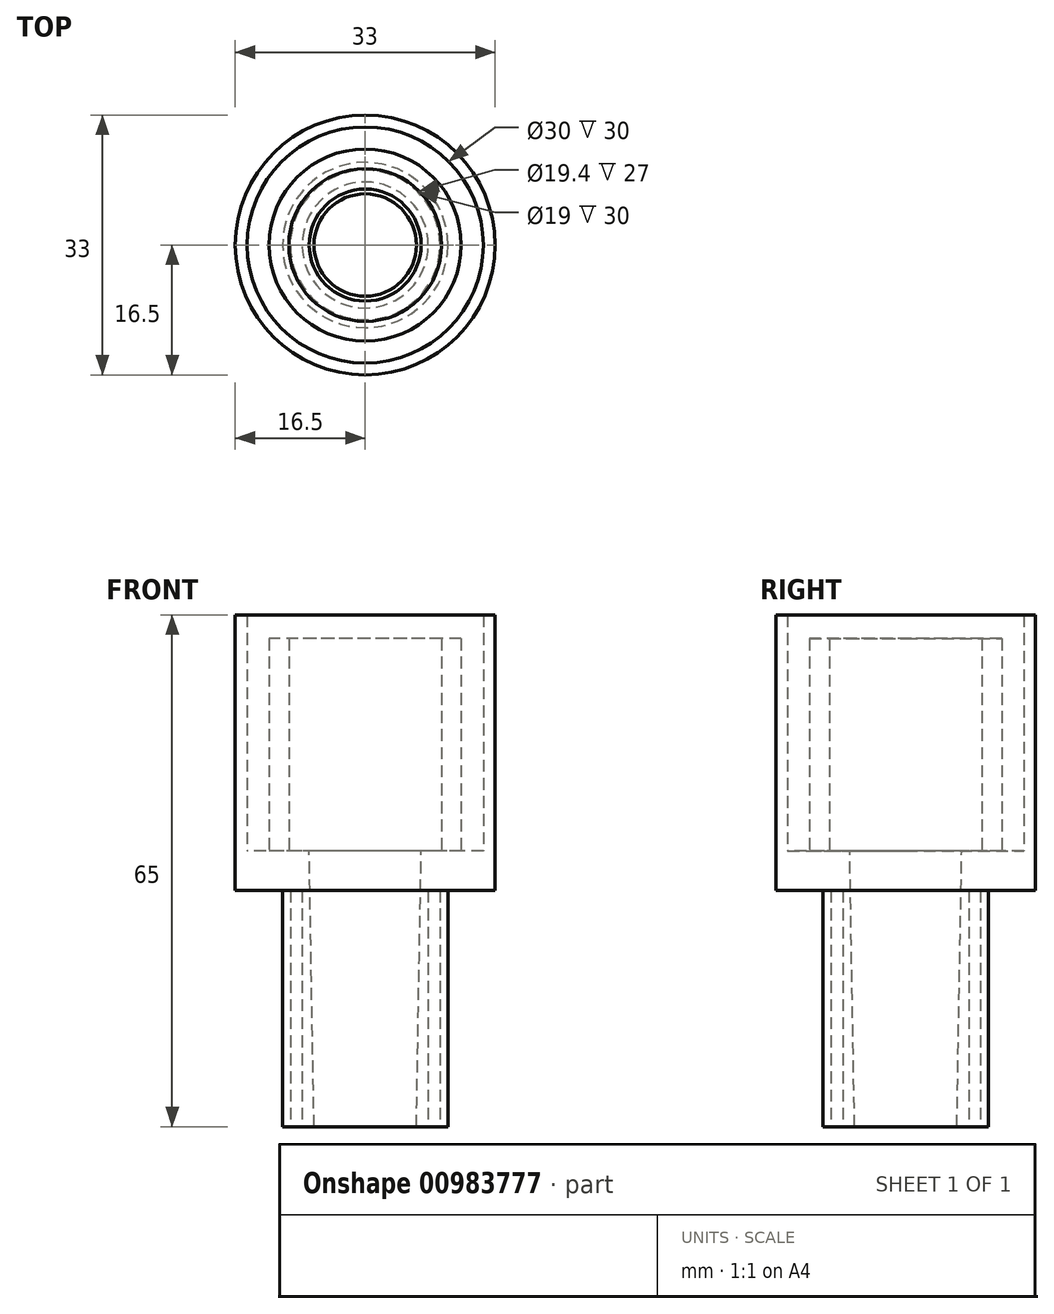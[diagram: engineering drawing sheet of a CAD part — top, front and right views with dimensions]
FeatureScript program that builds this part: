
annotation { "Feature Type Name" : "Feature", "Feature Type Description" : "" }
export const myFeature = defineFeature(function(context is Context, id is Id, definition is map)
    precondition{}
    {
        {
            var Q0;
            Q0=qCreatedBy(makeId("Top.planeOp"),FACE);
            var sketch = newSketch(context, id + "F0", { "sketchPlane" : qUnion([Q0])});
            skCircle(sketch, "E0", {"center": v(0, 0) * mm, "radius": 16.5 * mm});
            skSolve(sketch);
        }
        {
            var Q0;
            Q0 = qSketchRegion(id + "F0", true);
            extrude(context, id + "F1", {"entities" : qUnion([Q0]), "depth" : 5 * mm, "offsetDistance" : 25 * mm});
        }
        {
            var Q0;
            Q0=makeQuery(id+"F1.opExtrude","CAP_FACE",FACE,{"disambiguationData":[OSD([sQuery(id+"F0.wireOp",EDGE,"E0")])],"isStart":false});
            var sketch = newSketch(context, id + "F2", { "sketchPlane" : qUnion([Q0])});
            skCircle(sketch, "E1", {"center": v(0, 0) * mm, "radius": 15 * mm});
            skSolve(sketch);
        }
        {
            var Q0;
            Q0=makeQuery(id+"F2.imprint","IMPRINT",FACE,{"disambiguationData":[TD([[makeQuery(id+"F2.imprint","IMPRINT",EDGE,{"derivedFrom":sQuery(id+"F2.wireOp",EDGE,"E1")}),-1.0]])]});
            extrude(context, id + "F3", {"entities" : qUnion([Q0]), "operationType" : NewBodyOperationType.ADD, "depth" : 30 * mm, "offsetDistance" : 25 * mm});
        }
        {
            var Q0;
            Q0=makeQuery(id+"F1.opExtrude","CAP_FACE",FACE,{"disambiguationData":[OSD([sQuery(id+"F0.wireOp",EDGE,"E0")])],"isStart":false});
            var sketch = newSketch(context, id + "F4", { "sketchPlane" : qUnion([Q0])});
            skCircle(sketch, "E2", {"center": v(0, 0) * mm, "radius": 12.2 * mm});
            skCircle(sketch, "E3", {"center": v(0, 0) * mm, "radius": 9.7 * mm});
            skSolve(sketch);
        }
        {
            var Q0;
            Q0=makeQuery(id+"F4.imprint","IMPRINT",FACE,{"disambiguationData":[TD([[makeQuery(id+"F4.imprint","IMPRINT",EDGE,{"derivedFrom":sQuery(id+"F4.wireOp",EDGE,"E2")}),1.0]])]});
            extrude(context, id + "F5", {"entities" : qUnion([Q0]), "operationType" : NewBodyOperationType.ADD, "depth" : 27 * mm, "offsetDistance" : 25 * mm});
        }
        {
            var Q0;
            Q0=makeQuery(id+"F1.opExtrude","CAP_FACE",FACE,{"disambiguationData":[OSD([sQuery(id+"F0.wireOp",EDGE,"E0")])],"isStart":true});
            var sketch = newSketch(context, id + "F6", { "sketchPlane" : qUnion([Q0])});
            skCircle(sketch, "E4", {"center": v(0, 0) * mm, "radius": 10.5 * mm});
            skSolve(sketch);
        }
        {
            var Q0;
            Q0=makeQuery(id+"F6.imprint","IMPRINT",FACE,{"disambiguationData":[TD([[makeQuery(id+"F6.imprint","IMPRINT",EDGE,{"derivedFrom":sQuery(id+"F6.wireOp",EDGE,"E4")}),1.0]])]});
            extrude(context, id + "F7", {"entities" : qUnion([Q0]), "operationType" : NewBodyOperationType.ADD, "depth" : 30 * mm, "offsetDistance" : 25 * mm});
        }
        {
            var Q0;
            Q0=makeQuery(id+"F7.opExtrude","CAP_FACE",FACE,{"disambiguationData":[OSD([sQuery(id+"F6.wireOp",EDGE,"E4")])],"isStart":false});
            var sketch = newSketch(context, id + "F8", { "sketchPlane" : qUnion([Q0])});
            skCircle(sketch, "E5", {"center": v(0, 0) * mm, "radius": 9.5 * mm});
            skCircle(sketch, "E6", {"center": v(0, 0) * mm, "radius": 8 * mm});
            skCircle(sketch, "E7", {"center": v(0, 0) * mm, "radius": 6.5 * mm});
            skSolve(sketch);
        }
        {
            var Q0;
            Q0 = qSketchRegion(id + "F8", true);
            var Q1;
            Q1=makeQuery(id+"F8.imprint","IMPRINT",FACE,{"disambiguationData":[TD([[makeQuery(id+"F8.imprint","IMPRINT",EDGE,{"derivedFrom":sQuery(id+"F8.wireOp",EDGE,"E7")}),1.0]])]});
            extrude(context, id + "F9", {"entities" : qUnion([Q0, Q1]), "operationType" : NewBodyOperationType.REMOVE, "oppositeDirection" : true, "depth" : 30 * mm, "offsetDistance" : 25 * mm});
        }
        {
            var Q0;
            Q0=makeQuery(id+"F9.boolean.opBoolean","COPY",FACE,{"derivedFrom":makeQuery(id+"F9.opExtrude","CAP_FACE",FACE,{"disambiguationData":[OSD([sQuery(id+"F8.wireOp",EDGE,"E7")])],"isStart":false})});
            extrude(context, id + "F10", {"entities" : qUnion([Q0]), "operationType" : NewBodyOperationType.REMOVE, "oppositeDirection" : true, "depth" : 30 * mm, "offsetDistance" : 25 * mm});
        }
        {
            var Q0;
            Q0=makeQuery(id+"F10.boolean.opBoolean","INTERSECT",EDGE,{"derivedFrom":[makeQuery(id+"F5.boolean.opBoolean","SPLIT",FACE,{"disambiguationData":[TD([makeQuery(id+"F5.opExtrude","SWEPT_FACE",FACE,{"disambiguationData":[OSD([sQuery(id+"F4.wireOp",EDGE,"E3")])]})])],"derivedFrom":makeQuery(id+"F1.opExtrude","CAP_FACE",FACE,{"disambiguationData":[OSD([sQuery(id+"F0.wireOp",EDGE,"E0")])],"isStart":false})}),makeQuery(id+"F10.opExtrude","SWEPT_FACE",FACE,{"disambiguationData":[OSD([sQuery(id+"F8.wireOp",EDGE,"E7")])]})]});
            chamfer(context, id + "F11", {"entities" : qUnion([Q0]), "chamferType" : ChamferType.OFFSET_ANGLE, "width" : 35 * mm, "oppositeDirection" : false, "angle" : 1 * degree, "tangentPropagation" : true});
        }
    });
